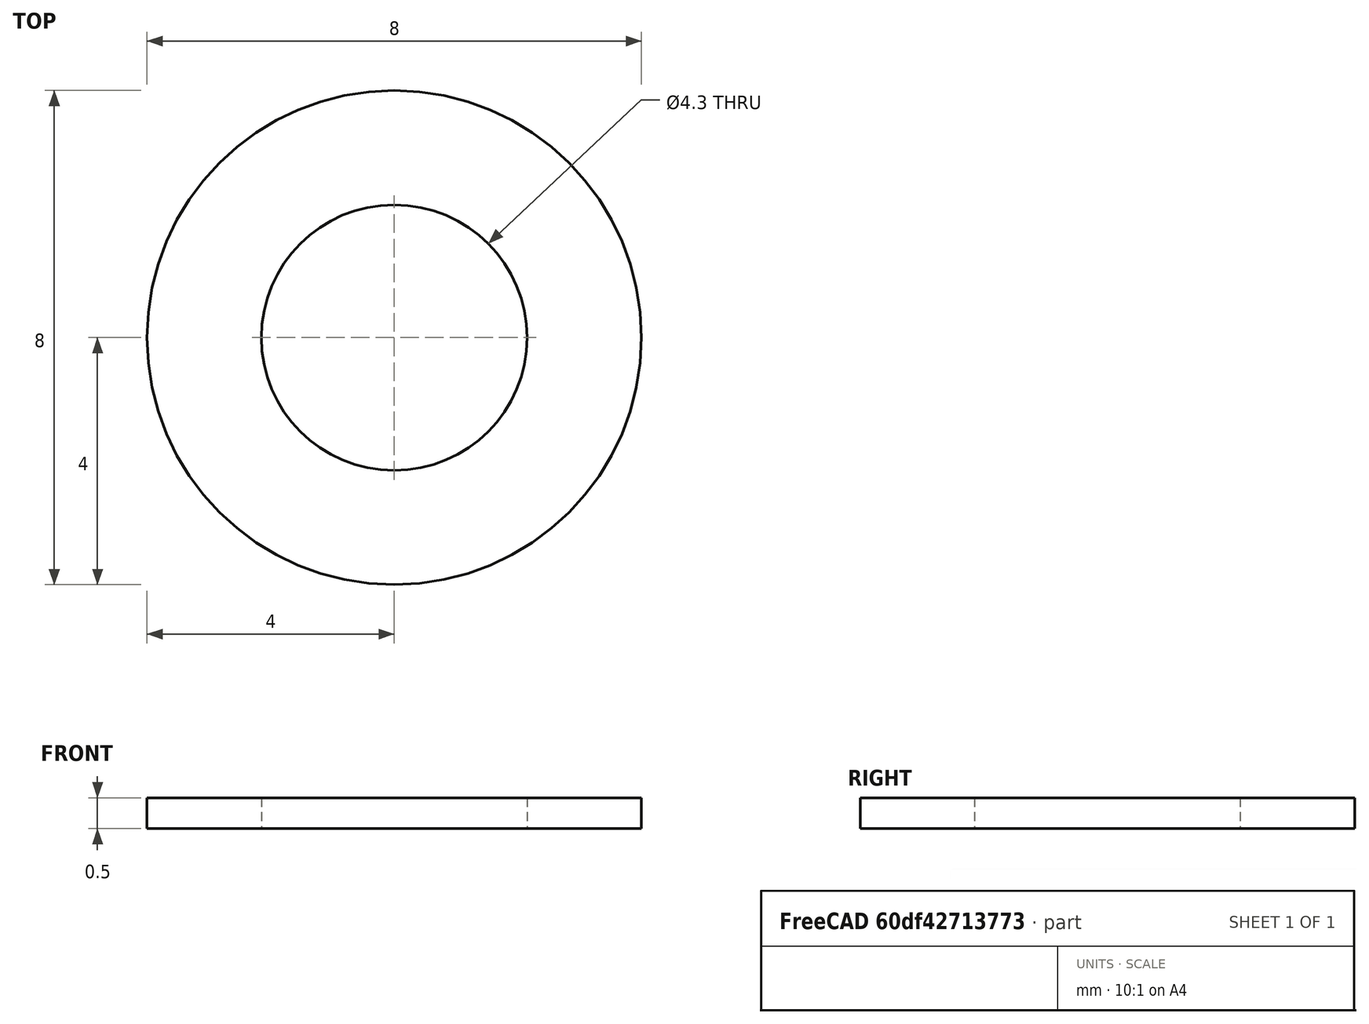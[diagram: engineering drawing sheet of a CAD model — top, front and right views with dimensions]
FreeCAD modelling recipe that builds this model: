
FCSTD DOCUMENT  (FreeCAD 0.14R3700 (Git))
Label: Scheibe DIN 433 - A 4,3
License: CC-BY 3.0
LicenseURL: http://creativecommons.org/licenses/by/3.0/
objects: Sketcher::SketchObject×1, PartDesign::Revolution×1, Part::Feature×1
note: 4 computed .brp shape members not serialized (recipe doc carries the construction recipe); baked Part::Feature solids carry a one-line shape summary decoded from their .brp

FEATURE [Sketcher::SketchObject] Sketch
  Placement = pos=(0,0,0) rot=(0.57735,0.57735,0.57735;2.0944rad)
  sketch-geometry (4):
    g0: LineSegment StartX=2.15 StartY=0 StartZ=0 EndX=4 EndY=0 EndZ=0
    g1: LineSegment StartX=4 StartY=0 StartZ=0 EndX=4 EndY=0.5 EndZ=0
    g2: LineSegment StartX=4 StartY=0.5 StartZ=0 EndX=2.15 EndY=0.5 EndZ=0
    g3: LineSegment StartX=2.15 StartY=0.5 StartZ=0 EndX=2.15 EndY=0 EndZ=0
  constraints (12):
    c: Coincident(g0,g1)
    c: Coincident(g1,g2)
    c: Coincident(g2,g3)
    c: Coincident(g3,g0)
    c: Horizontal(g0)
    c: Horizontal(g2)
    c: Vertical(g1)
    c: Vertical(g3)
    c: PointOnObject(g0,g-1)
    c: DistanceY(g1) = 0.5
    c: DistanceX(g-1,g2) = 2.15
    c: DistanceX(g-1,g1) = 4
FEATURE [PartDesign::Revolution] Revolution  label="Scheibe DIN 433 - A 4,3 #"
  Angle = 360
  Axis = (0,0,1)
  Base = (0,0,0)
  Placement = pos=(0,0,0) rot=(0.57735,0.57735,0.57735;2.0944rad)
  ReferenceAxis = -> Sketch [V_Axis]
  Reversed = true
  Sketch = -> Sketch
FEATURE [Part::Feature] Revolution001  label="Scheibe DIN 433 - A 4,3 #001"
  Placement = pos=(0,0,0) rot=(0.57735,0.57735,0.57735;2.0944rad)
  shape: bbox 8 x 8 x 0.5 mm, 4 faces (baked)
